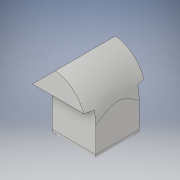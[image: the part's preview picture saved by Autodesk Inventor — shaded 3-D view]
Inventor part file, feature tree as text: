
AUTODESK INVENTOR PART (.ipt)
format: ipt  version: 2019 (Build 230136000, 136)  size: 169,472 bytes
history: native  units: mm
features: extrude x3, sketch x3, fillet x2, other x1, chamfer x1
ambient origin geometry x8: Origin, YZ Plane, XZ Plane, XY Plane, X Axis, Y Axis, Z Axis, Center Point
bodies: Body1 (feature_tree)
feature tree (10):
  other  "Твердое тело1"
  extrude  "Выдавливание1"  Depth=3.8mm
  extrude  "Выдавливание2"  Depth=3.8mm TaperAngle=0.0deg
  sketch  "Эскиз5"
  chamfer  "Фаска1"  Distance=5.25mm
  extrude  "Выдавливание3"  Depth=4.8mm
  fillet  "Сопряжение1"  Radius=2.0mm
  fillet  "Сопряжение2"  Radius=2.0mm
  sketch  "Эскиз1"
  sketch  "Эскиз2"
